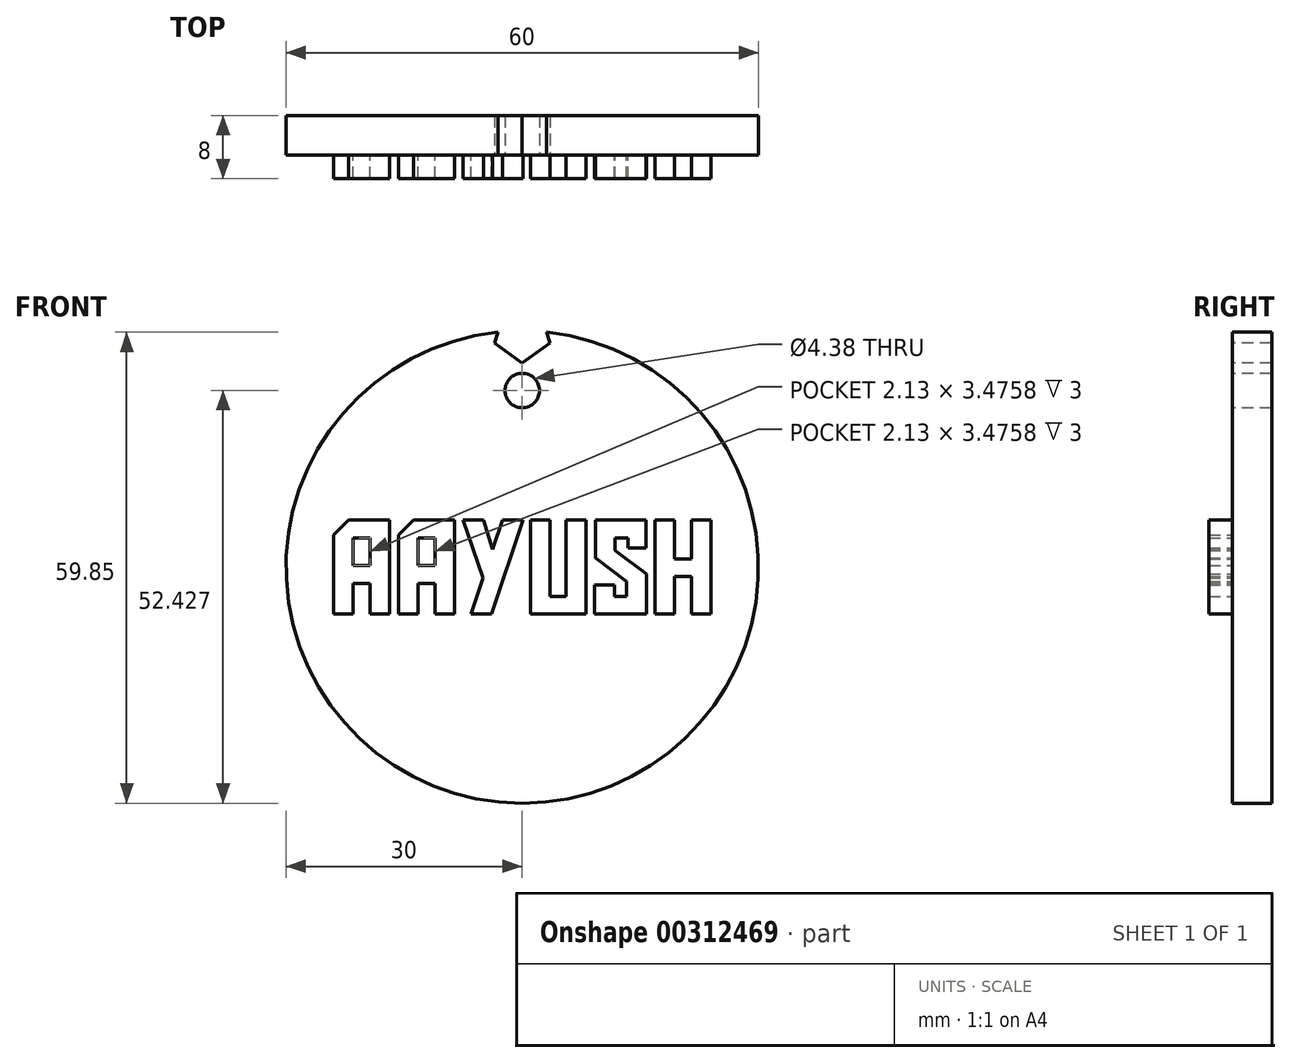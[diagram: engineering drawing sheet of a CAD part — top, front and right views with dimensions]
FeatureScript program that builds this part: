
annotation { "Feature Type Name" : "Feature", "Feature Type Description" : "" }
export const myFeature = defineFeature(function(context is Context, id is Id, definition is map)
    precondition{}
    {
        {
            var Q0;
            Q0=qCreatedBy(makeId("Top.planeOp"),FACE);
            var sketch = newSketch(context, id + "F0", { "sketchPlane" : qUnion([Q0])});
            skLineSegment(sketch, "E0.bottom", {"start": v(0, 0) * mm, "end": v(-30, 0) * mm});
            skLineSegment(sketch, "E0.top", {"start": v(0, 5) * mm, "end": v(-30, 5) * mm});
            skLineSegment(sketch, "E0.left", {"start": v(0, 0) * mm, "end": v(0, 5) * mm});
            skLineSegment(sketch, "E0.right", {"start": v(-30, 0) * mm, "end": v(-30, 5) * mm});
            skSolve(sketch);
        }
        {
            var Q0;
            Q0 = qSketchRegion(id + "F0", true);
            var Q1;
            Q1=sQuery(id+"F0.wireOp",EDGE,"E0.left");
            revolve(context, id + "F1", {"entities" : qUnion([Q0]), "axis" : qUnion([Q1]), "revolveType" : RevolveType.FULL});
        }
        {
            var Q0;
            Q0=qCreatedBy(makeId("Front.planeOp"),FACE);
            var sketch = newSketch(context, id + "F2", { "sketchPlane" : qUnion([Q0])});
            skLineSegment(sketch, "E1", {"start": v(-21.5, -5.97) * mm, "end": v(-24, -5.97) * mm});
            skLineSegment(sketch, "E2", {"start": v(-24, -5.97) * mm, "end": v(-24, 4.08) * mm});
            skLineSegment(sketch, "E3", {"start": v(-24, 4.08) * mm, "end": v(-22.08, 5.97) * mm});
            skLineSegment(sketch, "E4", {"start": v(-22.08, 5.97) * mm, "end": v(-16.86, 5.97) * mm});
            skLineSegment(sketch, "E5", {"start": v(-16.86, 5.97) * mm, "end": v(-16.86, -5.97) * mm});
            skLineSegment(sketch, "E6", {"start": v(-16.86, -5.97) * mm, "end": v(-19.36, -5.97) * mm});
            skLineSegment(sketch, "E7", {"start": v(-19.36, -5.97) * mm, "end": v(-19.36, -2.05) * mm});
            skLineSegment(sketch, "E8", {"start": v(-19.36, -2.05) * mm, "end": v(-21.5, -2.05) * mm});
            skLineSegment(sketch, "E9", {"start": v(-21.5, -2.05) * mm, "end": v(-21.5, -5.97) * mm});
            skLineSegment(sketch, "E10", {"start": v(-19.36, 0.22) * mm, "end": v(-19.36, 3.7) * mm});
            skLineSegment(sketch, "E11", {"start": v(-19.36, 3.7) * mm, "end": v(-21.5, 3.7) * mm});
            skLineSegment(sketch, "E12", {"start": v(-21.5, 3.7) * mm, "end": v(-21.5, 0.22) * mm});
            skLineSegment(sketch, "E13", {"start": v(-21.5, 0.22) * mm, "end": v(-19.36, 0.22) * mm});
            skLineSegment(sketch, "E14", {"start": v(-13.23, -5.97) * mm, "end": v(-15.74, -5.97) * mm});
            skLineSegment(sketch, "E15", {"start": v(-15.74, -5.97) * mm, "end": v(-15.74, 4.08) * mm});
            skLineSegment(sketch, "E16", {"start": v(-15.74, 4.08) * mm, "end": v(-13.82, 5.97) * mm});
            skLineSegment(sketch, "E17", {"start": v(-13.82, 5.97) * mm, "end": v(-8.6, 5.97) * mm});
            skLineSegment(sketch, "E18", {"start": v(-8.6, 5.97) * mm, "end": v(-8.6, -5.97) * mm});
            skLineSegment(sketch, "E19", {"start": v(-8.6, -5.97) * mm, "end": v(-11.1, -5.97) * mm});
            skLineSegment(sketch, "E20", {"start": v(-11.1, -5.97) * mm, "end": v(-11.1, -2.05) * mm});
            skLineSegment(sketch, "E21", {"start": v(-11.1, -2.05) * mm, "end": v(-13.23, -2.05) * mm});
            skLineSegment(sketch, "E22", {"start": v(-13.23, -2.05) * mm, "end": v(-13.23, -5.97) * mm});
            skLineSegment(sketch, "E23", {"start": v(-11.1, 0.22) * mm, "end": v(-11.1, 3.7) * mm});
            skLineSegment(sketch, "E24", {"start": v(-11.1, 3.7) * mm, "end": v(-13.23, 3.7) * mm});
            skLineSegment(sketch, "E25", {"start": v(-13.23, 3.7) * mm, "end": v(-13.23, 0.22) * mm});
            skLineSegment(sketch, "E26", {"start": v(-13.23, 0.22) * mm, "end": v(-11.1, 0.22) * mm});
            skLineSegment(sketch, "E27", {"start": v(-2.5, 5.97) * mm, "end": v(0.1, 5.97) * mm});
            skLineSegment(sketch, "E28", {"start": v(0.1, 5.97) * mm, "end": v(-3.93, -5.97) * mm});
            skLineSegment(sketch, "E29", {"start": v(-3.93, -5.97) * mm, "end": v(-6.54, -5.97) * mm});
            skLineSegment(sketch, "E30", {"start": v(-6.54, -5.97) * mm, "end": v(-5, -1.4) * mm});
            skLineSegment(sketch, "E31", {"start": v(-5, -1.4) * mm, "end": v(-7.5, 5.97) * mm});
            skLineSegment(sketch, "E32", {"start": v(-7.5, 5.97) * mm, "end": v(-4.91, 5.97) * mm});
            skLineSegment(sketch, "E33", {"start": v(-4.91, 5.97) * mm, "end": v(-3.76, 2.27) * mm});
            skLineSegment(sketch, "E34", {"start": v(-3.76, 2.27) * mm, "end": v(-2.5, 5.97) * mm});
            skLineSegment(sketch, "E35", {"start": v(8.1, -5.97) * mm, "end": v(1.03, -5.97) * mm});
            skLineSegment(sketch, "E36", {"start": v(1.03, -5.97) * mm, "end": v(1.03, 5.97) * mm});
            skLineSegment(sketch, "E37", {"start": v(1.03, 5.97) * mm, "end": v(3.53, 5.97) * mm});
            skLineSegment(sketch, "E38", {"start": v(3.53, 5.97) * mm, "end": v(3.53, -3.7) * mm});
            skLineSegment(sketch, "E39", {"start": v(3.53, -3.7) * mm, "end": v(5.58, -3.7) * mm});
            skLineSegment(sketch, "E40", {"start": v(5.58, -3.7) * mm, "end": v(5.58, 5.97) * mm});
            skLineSegment(sketch, "E41", {"start": v(5.58, 5.97) * mm, "end": v(8.1, 5.97) * mm});
            skLineSegment(sketch, "E42", {"start": v(8.1, 5.97) * mm, "end": v(8.1, -5.97) * mm});
            skLineSegment(sketch, "E43", {"start": v(15.77, -5.97) * mm, "end": v(9.2, -5.97) * mm});
            skLineSegment(sketch, "E44", {"start": v(9.2, -5.97) * mm, "end": v(9.2, -2.25) * mm});
            skLineSegment(sketch, "E45", {"start": v(9.2, -2.25) * mm, "end": v(11.7, -2.25) * mm});
            skLineSegment(sketch, "E46", {"start": v(11.7, -2.25) * mm, "end": v(11.7, -3.7) * mm});
            skLineSegment(sketch, "E47", {"start": v(11.7, -3.7) * mm, "end": v(13.26, -3.7) * mm});
            skLineSegment(sketch, "E48", {"start": v(13.26, -3.7) * mm, "end": v(13.26, -1.8) * mm});
            skLineSegment(sketch, "E49", {"start": v(13.26, -1.8) * mm, "end": v(9.29, 1.19) * mm});
            skLineSegment(sketch, "E50", {"start": v(9.29, 1.19) * mm, "end": v(9.29, 5.97) * mm});
            skLineSegment(sketch, "E51", {"start": v(9.29, 5.97) * mm, "end": v(15.7, 5.97) * mm});
            skLineSegment(sketch, "E52", {"start": v(15.7, 5.97) * mm, "end": v(15.7, 2.42) * mm});
            skLineSegment(sketch, "E53", {"start": v(15.7, 2.42) * mm, "end": v(13.42, 2.42) * mm});
            skLineSegment(sketch, "E54", {"start": v(13.42, 2.42) * mm, "end": v(13.42, 3.7) * mm});
            skLineSegment(sketch, "E55", {"start": v(13.42, 3.7) * mm, "end": v(11.79, 3.7) * mm});
            skLineSegment(sketch, "E56", {"start": v(11.79, 3.7) * mm, "end": v(11.79, 2.13) * mm});
            skLineSegment(sketch, "E57", {"start": v(11.79, 2.13) * mm, "end": v(15.77, -0.86) * mm});
            skLineSegment(sketch, "E58", {"start": v(15.77, -0.86) * mm, "end": v(15.77, -5.97) * mm});
            skLineSegment(sketch, "E59", {"start": v(19.35, 1.07) * mm, "end": v(21.5, 1.07) * mm});
            skLineSegment(sketch, "E60", {"start": v(21.5, 1.07) * mm, "end": v(21.5, 5.97) * mm});
            skLineSegment(sketch, "E61", {"start": v(21.5, 5.97) * mm, "end": v(24, 5.97) * mm});
            skLineSegment(sketch, "E62", {"start": v(24, 5.97) * mm, "end": v(24, -5.97) * mm});
            skLineSegment(sketch, "E63", {"start": v(24, -5.97) * mm, "end": v(21.5, -5.97) * mm});
            skLineSegment(sketch, "E64", {"start": v(21.5, -5.97) * mm, "end": v(21.5, -1.2) * mm});
            skLineSegment(sketch, "E65", {"start": v(21.5, -1.2) * mm, "end": v(19.35, -1.2) * mm});
            skLineSegment(sketch, "E66", {"start": v(19.35, -1.2) * mm, "end": v(19.35, -5.97) * mm});
            skLineSegment(sketch, "E67", {"start": v(19.35, -5.97) * mm, "end": v(16.85, -5.97) * mm});
            skLineSegment(sketch, "E68", {"start": v(16.85, -5.97) * mm, "end": v(16.85, 5.97) * mm});
            skLineSegment(sketch, "E69", {"start": v(16.85, 5.97) * mm, "end": v(19.35, 5.97) * mm});
            skLineSegment(sketch, "E70", {"start": v(19.35, 5.97) * mm, "end": v(19.35, 1.07) * mm});
            skSolve(sketch);
        }
        {
            var Q0;
            Q0 = qSketchRegion(id + "F2", true);
            extrude(context, id + "F3", {"entities" : qUnion([Q0]), "operationType" : NewBodyOperationType.ADD, "depth" : 3 * mm});
        }
        {
            var Q0;
            Q0=qCreatedBy(makeId("Front.planeOp"),FACE);
            var sketch = newSketch(context, id + "F4", { "sketchPlane" : qUnion([Q0])});
            skCircle(sketch, "E71.cCircle", {"center": v(0, 29.62) * mm, "radius": 2.98 * mm, "construction": true});
            skLineSegment(sketch, "E71.0", {"start": v(-2.16, 32.6) * mm, "end": v(2.16, 32.6) * mm});
            skLineSegment(sketch, "E71.1", {"start": v(2.16, 32.6) * mm, "end": v(3.5, 28.48) * mm});
            skLineSegment(sketch, "E71.2", {"start": v(3.5, 28.48) * mm, "end": v(0, 25.94) * mm});
            skLineSegment(sketch, "E71.3", {"start": v(0, 25.94) * mm, "end": v(-3.5, 28.48) * mm});
            skLineSegment(sketch, "E71.4", {"start": v(-3.5, 28.48) * mm, "end": v(-2.16, 32.6) * mm});
            skPoint(sketch, "E71.0.midPoint", {"position": v(0, 32.6) * mm});
            skSolve(sketch);
        }
        {
            var Q0;
            Q0 = qSketchRegion(id + "F4", true);
            extrude(context, id + "F5", {"entities" : qUnion([Q0]), "operationType" : NewBodyOperationType.REMOVE, "oppositeDirection" : true, "depth" : 25.4 * mm});
        }
        {
            var Q0;
            Q0=qCreatedBy(makeId("Front.planeOp"),FACE);
            var sketch = newSketch(context, id + "F6", { "sketchPlane" : qUnion([Q0])});
            skCircle(sketch, "E72", {"center": v(0, 22.43) * mm, "radius": 2.2 * mm});
            skSolve(sketch);
        }
        {
            var Q0;
            Q0 = qSketchRegion(id + "F6", true);
            extrude(context, id + "F7", {"entities" : qUnion([Q0]), "operationType" : NewBodyOperationType.REMOVE, "oppositeDirection" : true, "depth" : 25.4 * mm});
        }
    });
